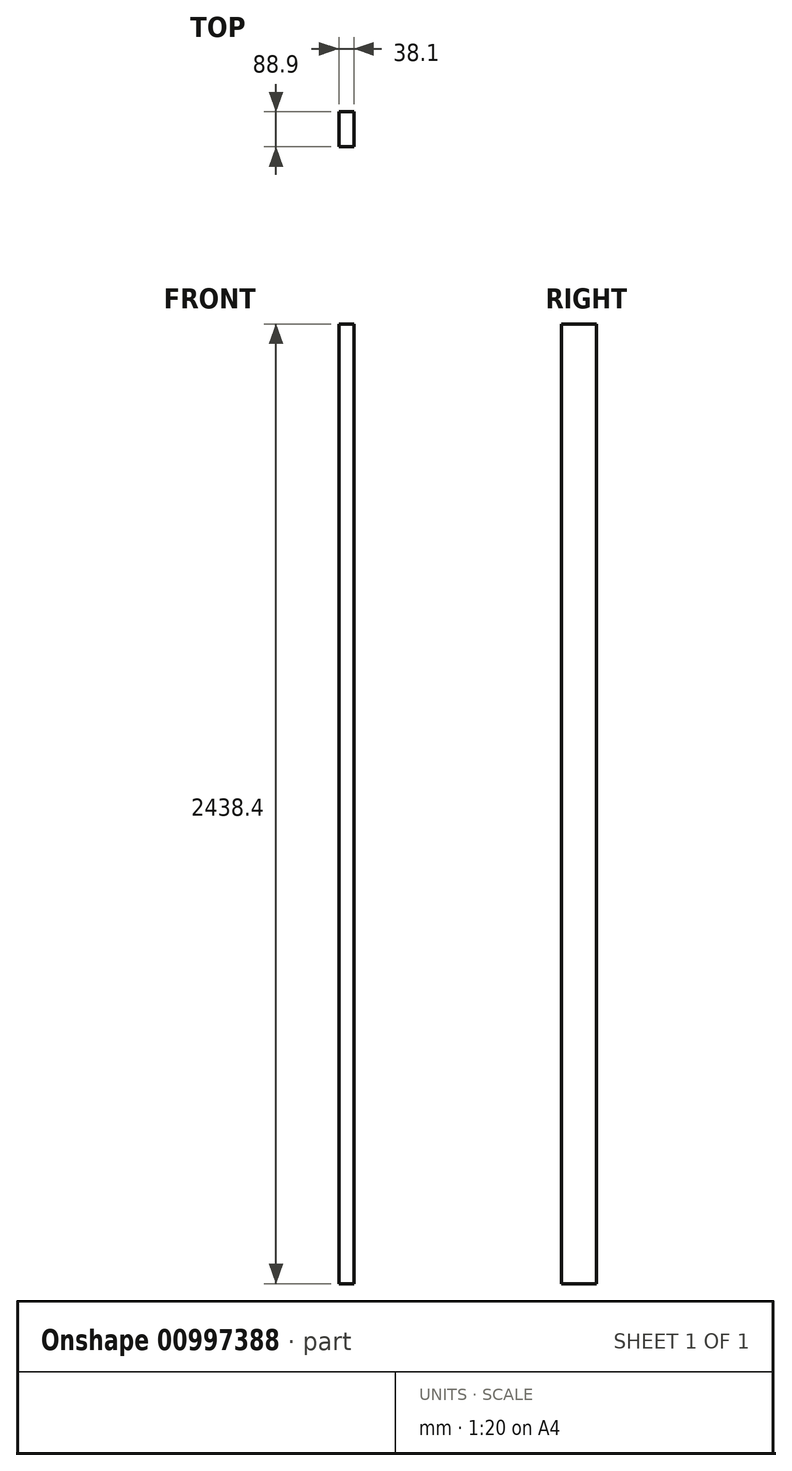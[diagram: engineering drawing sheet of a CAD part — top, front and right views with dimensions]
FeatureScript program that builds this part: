
annotation { "Feature Type Name" : "Feature", "Feature Type Description" : "" }
export const myFeature = defineFeature(function(context is Context, id is Id, definition is map)
    precondition{}
    {
        {
            var Q0;
            Q0=qCreatedBy(makeId("Top.planeOp"),FACE);
            var sketch = newSketch(context, id + "F0", { "sketchPlane" : qUnion([Q0])});
            skLineSegment(sketch, "E0.bottom", {"start": v(-15.69, 0) * mm, "end": v(22.41, 0) * mm});
            skLineSegment(sketch, "E0.top", {"start": v(-15.69, -88.9) * mm, "end": v(22.41, -88.9) * mm});
            skLineSegment(sketch, "E0.left", {"start": v(-15.69, 0) * mm, "end": v(-15.69, -88.9) * mm});
            skLineSegment(sketch, "E0.right", {"start": v(22.41, 0) * mm, "end": v(22.41, -88.9) * mm});
            skSolve(sketch);
        }
        {
            var Q0;
            Q0 = qSketchRegion(id + "F0", true);
            extrude(context, id + "F1", {"entities" : qUnion([Q0]), "depth" : 2438.4 * mm, "offsetDistance" : 25.4 * mm});
        }
    });
